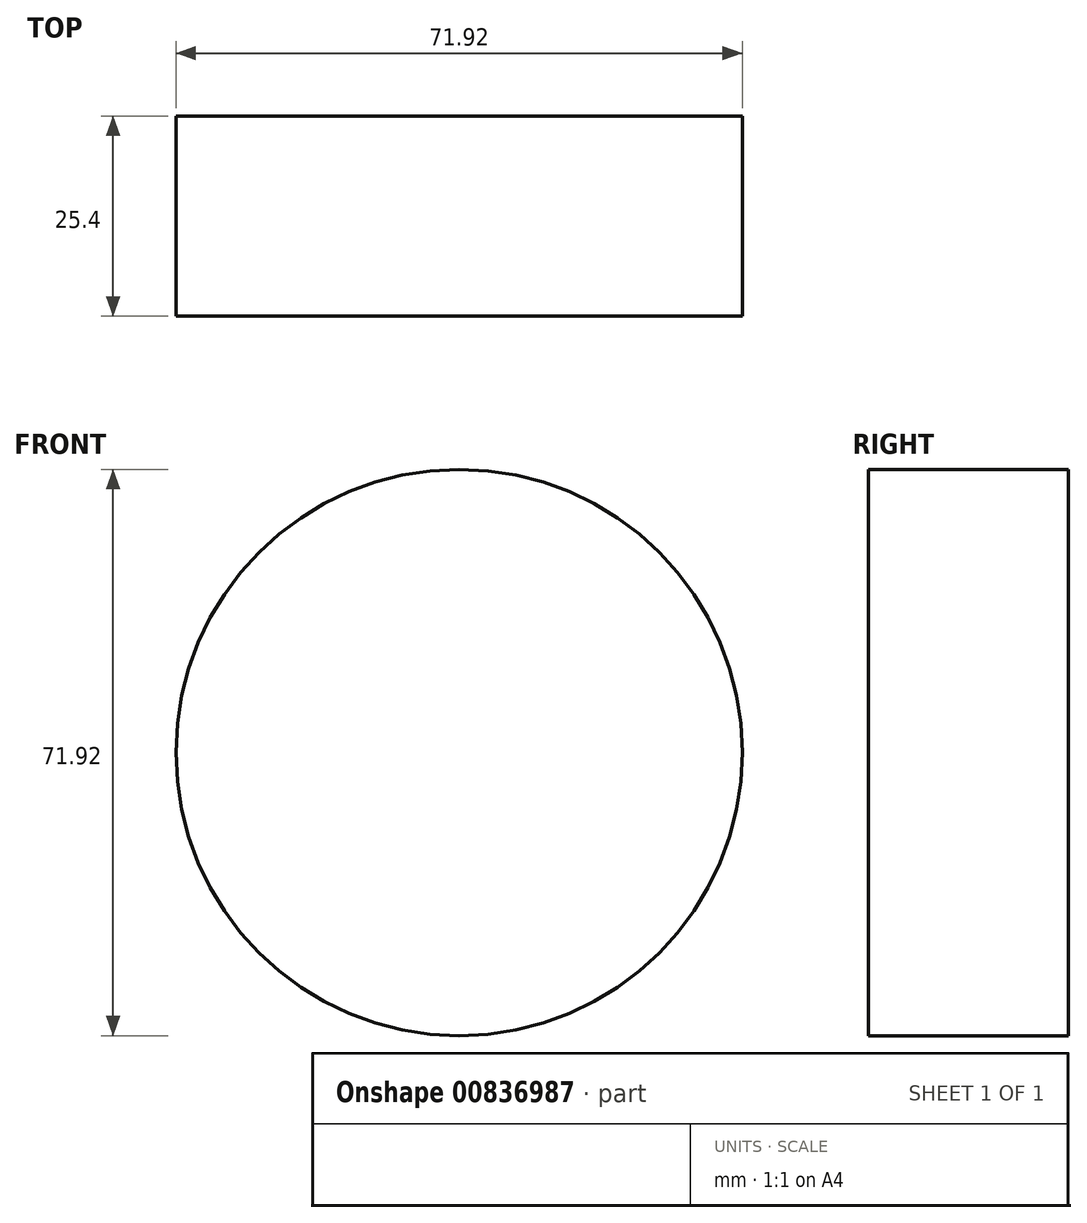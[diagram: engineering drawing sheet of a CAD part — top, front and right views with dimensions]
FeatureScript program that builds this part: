
annotation { "Feature Type Name" : "Feature", "Feature Type Description" : "" }
export const myFeature = defineFeature(function(context is Context, id is Id, definition is map)
    precondition{}
    {
        {
            var Q0;
            Q0=qCreatedBy(makeId("Front.planeOp"),FACE);
            var sketch = newSketch(context, id + "F0", { "sketchPlane" : qUnion([Q0])});
            skCircle(sketch, "E0", {"center": v(0, 0) * mm, "radius": 35.96 * mm});
            skSolve(sketch);
        }
        {
            var Q0;
            Q0 = qSketchRegion(id + "F0", true);
            extrude(context, id + "F1", {"entities" : qUnion([Q0]), "depth" : 25.4 * mm, "offsetDistance" : 25.4 * mm});
        }
    });
